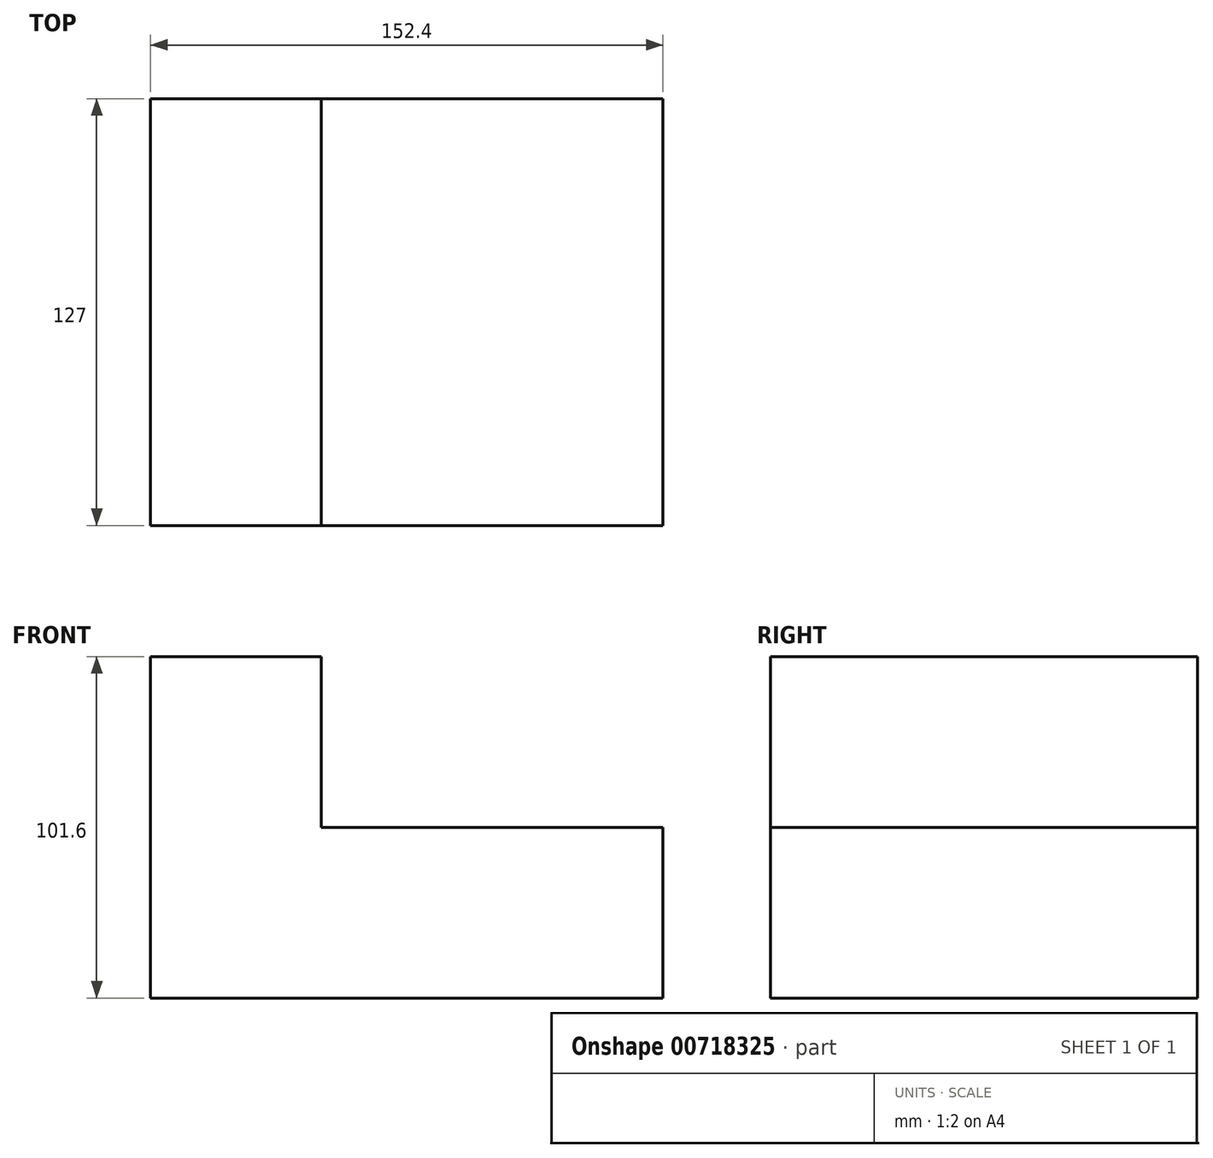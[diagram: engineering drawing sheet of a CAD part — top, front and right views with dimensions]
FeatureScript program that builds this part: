
annotation { "Feature Type Name" : "Feature", "Feature Type Description" : "" }
export const myFeature = defineFeature(function(context is Context, id is Id, definition is map)
    precondition{}
    {
        {
            var Q0;
            Q0=qCreatedBy(makeId("Front.planeOp"),FACE);
            var sketch = newSketch(context, id + "F0", { "sketchPlane" : qUnion([Q0])});
            skLineSegment(sketch, "E0", {"start": v(-75.89, -56.34) * mm, "end": v(76.51, -56.34) * mm});
            skLineSegment(sketch, "E1", {"start": v(76.51, -56.34) * mm, "end": v(76.51, -5.54) * mm});
            skLineSegment(sketch, "E2", {"start": v(76.51, -5.54) * mm, "end": v(-25.09, -5.54) * mm});
            skLineSegment(sketch, "E3", {"start": v(-25.09, -5.54) * mm, "end": v(-25.09, 45.26) * mm});
            skLineSegment(sketch, "E4", {"start": v(-25.09, 45.26) * mm, "end": v(-75.89, 45.26) * mm});
            skLineSegment(sketch, "E5", {"start": v(-75.89, 45.26) * mm, "end": v(-75.89, -56.34) * mm});
            skSolve(sketch);
        }
        {
            var Q0;
            Q0 = qSketchRegion(id + "F0", true);
            var Q1;
            Q1 = qSketchRegion(id + "FOBQZCzXuLWjLXd_0", true);
            extrude(context, id + "F1", {"entities" : qUnion([Q0, Q1]), "depth" : 127 * mm, "offsetDistance" : 25.4 * mm});
        }
    });
